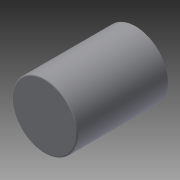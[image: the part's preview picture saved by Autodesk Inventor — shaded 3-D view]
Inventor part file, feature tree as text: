
AUTODESK INVENTOR PART (.ipt)
format: ipt  version: 2015 (Build 190159000, 159)  size: 96,256 bytes
history: native  units: mm
features: extrude x1, shell x1, fillet x1, sketch x1
ambient origin geometry x8: Origin, YZ Plane, XZ Plane, XY Plane, X Axis, Y Axis, Z Axis, Center Point
bodies: Solid1 (feature_tree)
feature tree (4):
  extrude  "Extrusion1"  Depth=140.0mm TaperAngle=0.0deg
  shell  "Shell1"  Thickness=5.0mm
  fillet  "Fillet1"  Radius=2.0mm
  sketch  "Sketch1"  dims[d0=100.0mm d1=140.0mm d2=0.0mm d3=5.0mm d4=2.0mm]
